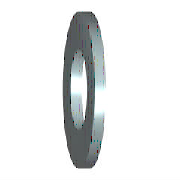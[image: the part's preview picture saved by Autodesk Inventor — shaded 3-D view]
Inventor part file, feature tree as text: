
AUTODESK INVENTOR PART (.ipt)
format: ipt  version: 2020 (Build 240168000, 168)  size: 110,592 bytes
history: native  units: mm (DEFAULTED — no unit token found)
features: other x1, plane x1, sketch x1
ambient origin geometry x7: Origin, YZ Plane, XY Plane, X Axis, Y Axis, Z Axis, Center Point
bodies: Solid1 (feature_tree), Body (feature_tree)
feature tree (3):
  other  "Work Axis1"
  plane  "Work Plane1"
  sketch  "Sketch"  dims[d0=5.3mm d1=10.0mm d2=1.0mm d3=0.0mm d4=0.0mm d5=0.0mm d6=0.0mm d7=0.0mm]
